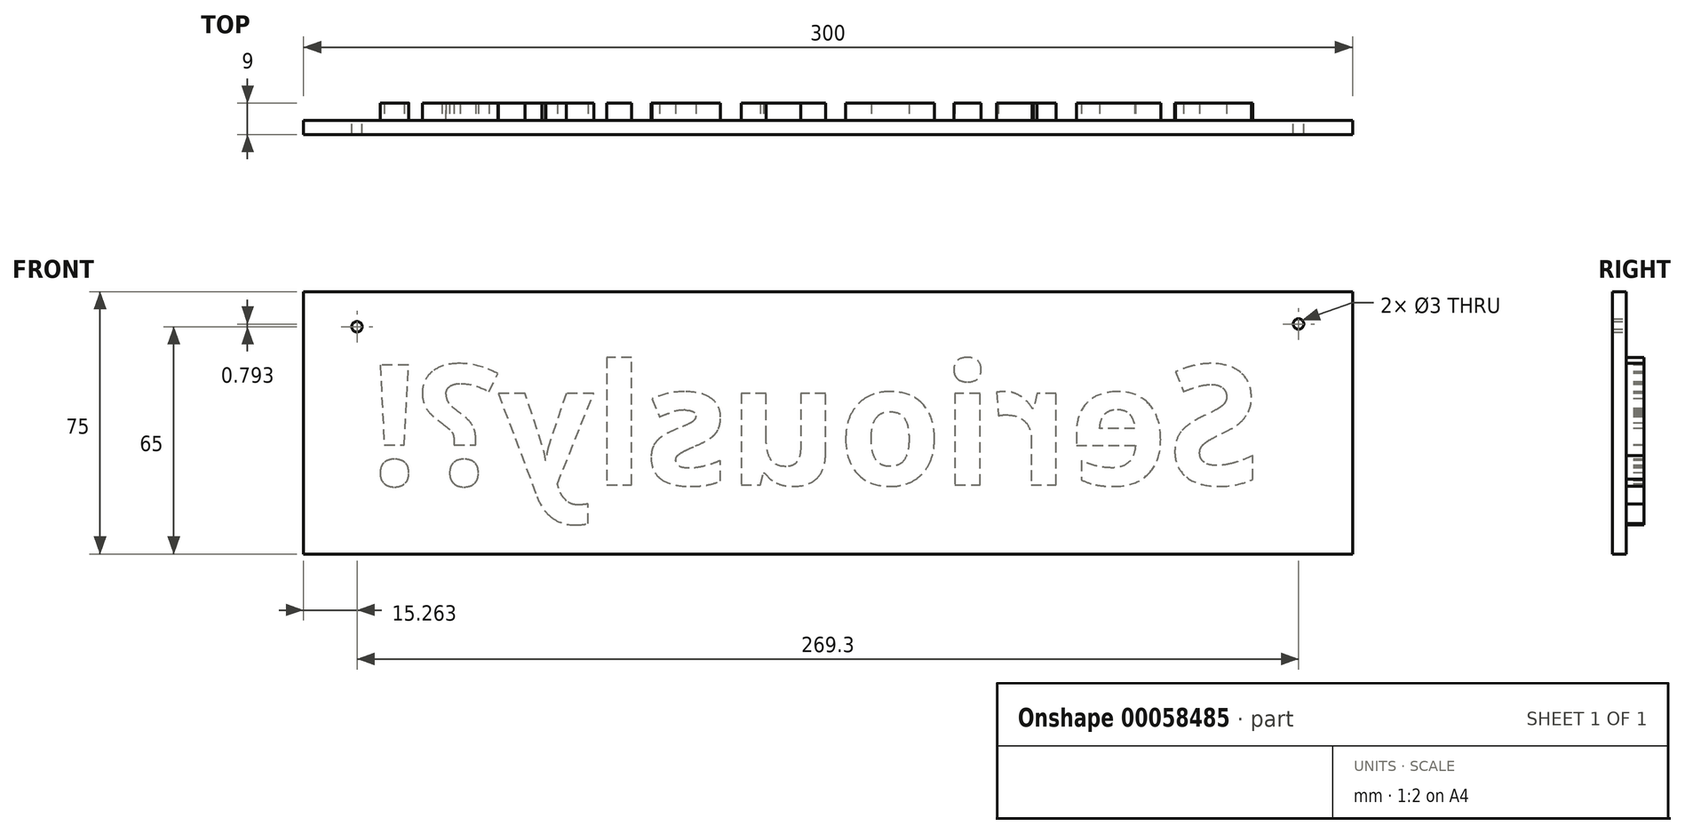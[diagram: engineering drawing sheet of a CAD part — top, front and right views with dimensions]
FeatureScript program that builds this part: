
annotation { "Feature Type Name" : "Feature", "Feature Type Description" : "" }
export const myFeature = defineFeature(function(context is Context, id is Id, definition is map)
    precondition{}
    {
        {
            var Q0;
            Q0=qCreatedBy(makeId("Front.planeOp"),FACE);
            var sketch = newSketch(context, id + "F0", { "sketchPlane" : qUnion([Q0])});
            skLineSegment(sketch, "E0.bottom", {"start": v(0, 0) * mm, "end": v(300, 0) * mm});
            skLineSegment(sketch, "E0.top", {"start": v(0, 75) * mm, "end": v(300, 75) * mm});
            skLineSegment(sketch, "E0.left", {"start": v(0, 0) * mm, "end": v(0, 75) * mm});
            skLineSegment(sketch, "E0.right", {"start": v(300, 0) * mm, "end": v(300, 75) * mm});
            skSolve(sketch);
        }
        {
            var Q0;
            Q0=makeQuery(id+"F0.imprint","IMPRINT",FACE,{"disambiguationData":[TD([[makeQuery(id+"F0.imprint","IMPRINT",EDGE,{"derivedFrom":sQuery(id+"F0.wireOp",EDGE,"E0.bottom")}),1.0]])]});
            extrude(context, id + "F1", {"entities" : qUnion([Q0]), "depth" : 4 * mm});
        }
        {
            var Q0;
            Q0=makeQuery(id+"F1.opExtrude","CAP_FACE",FACE,{"disambiguationData":[OSD([sQuery(id+"F0.wireOp",EDGE,"E0.bottom"),sQuery(id+"F0.wireOp",EDGE,"E0.top"),sQuery(id+"F0.wireOp",EDGE,"E0.left"),sQuery(id+"F0.wireOp",EDGE,"E0.right")])],"isStart":true});
            var sketch = newSketch(context, id + "F2", { "sketchPlane" : qUnion([Q0])});
            skText(sketch, "E1", { "text": "Seriously?!", "fontName": "OpenSans-Bold.ttf"});
            const initialGuessF2  = {"E1": [-0.27368, 0.01981, 1, 0, 0.03451]};
            skSetInitialGuess(sketch, initialGuessF2);
            skSolve(sketch);
        }
        {
            var Q0;
            Q0=makeQuery(id+"F2.imprint","IMPRINT",FACE,{"disambiguationData":[TD([[makeQuery(id+"F2.imprint","IMPRINT",EDGE,{"derivedFrom":sQuery(id+"F2.wireOp",EDGE,"E1.sketch_text.stroke-0")}),-1.0]])]});
            var Q1;
            Q1 = qSketchRegion(id + "F2", true);
            var Q2;
            Q2=makeQuery(id+"F2.imprint","IMPRINT",FACE,{"disambiguationData":[TD([[makeQuery(id+"F2.imprint","IMPRINT",EDGE,{"derivedFrom":sQuery(id+"F2.wireOp",EDGE,"E1.sketch_text.stroke-135")}),-1.0]])]});
            extrude(context, id + "F3", {"entities" : qUnion([Q0, Q1, Q2]), "operationType" : NewBodyOperationType.ADD, "depth" : 5 * mm});
        }
        {
            var Q0;
            {var subQ0=sQuery(id+"F0.wireOp",EDGE,"E0.left");var subQ1=sQuery(id+"F0.wireOp",EDGE,"E0.bottom");var subQ2=sQuery(id+"F0.wireOp",EDGE,"E0.right");var subQ3=sQuery(id+"F0.wireOp",EDGE,"E0.top");Q0=makeQuery(id+"F3.boolean.opBoolean","SPLIT",FACE,{"disambiguationData":[TD([makeQuery(id+"F1.opExtrude","SWEPT_FACE",FACE,{"disambiguationData":[OSD([subQ1])]})])],"derivedFrom":makeQuery(id+"F1.opExtrude","CAP_FACE",FACE,{"disambiguationData":[OSD([subQ1,subQ3,subQ0,subQ2])],"isStart":true})});}
            var sketch = newSketch(context, id + "F4", { "sketchPlane" : qUnion([Q0])});
            skPoint(sketch, "E2", {"position": v(-284.56, 65.8) * mm});
            skPoint(sketch, "E3", {"position": v(-10.99, 65.8) * mm});
            skSolve(sketch);
        }
        {
            var Q0;
            Q0=sQuery(id+"F4.wireOp",VERTEX,"E2");
            var Q1;
            Q1=makeQuery(id+"F1.opExtrude","SWEPT_BODY",BODY,{"disambiguationData":[OSD([sQuery(id+"F0.wireOp",EDGE,"E0.bottom"),sQuery(id+"F0.wireOp",EDGE,"E0.top"),sQuery(id+"F0.wireOp",EDGE,"E0.left"),sQuery(id+"F0.wireOp",EDGE,"E0.right")])]});
            hole(context, id + "F5", {"style" : HoleStyle.SIMPLE, "holeDiameter" : 3 * mm, "endStyle" : HoleEndStyle.THROUGH, "locations" : qUnion([Q0]), "scope" : qUnion([Q1])});
        }
        {
            var Q0;
            {var subQ0=sQuery(id+"F0.wireOp",EDGE,"E0.left");var subQ1=sQuery(id+"F0.wireOp",EDGE,"E0.bottom");var subQ2=sQuery(id+"F0.wireOp",EDGE,"E0.right");var subQ3=sQuery(id+"F0.wireOp",EDGE,"E0.top");Q0=makeQuery(id+"F3.boolean.opBoolean","SPLIT",FACE,{"disambiguationData":[TD([makeQuery(id+"F1.opExtrude","SWEPT_FACE",FACE,{"disambiguationData":[OSD([subQ1])]})])],"derivedFrom":makeQuery(id+"F1.opExtrude","CAP_FACE",FACE,{"disambiguationData":[OSD([subQ1,subQ3,subQ0,subQ2])],"isStart":true})});}
            var sketch = newSketch(context, id + "F6", { "sketchPlane" : qUnion([Q0])});
            skPoint(sketch, "E4", {"position": v(-15.26, 65) * mm});
            skSolve(sketch);
        }
        {
            var Q0;
            Q0=sQuery(id+"F6.wireOp",VERTEX,"E4");
            var Q1;
            Q1=makeQuery(id+"F1.opExtrude","SWEPT_BODY",BODY,{"disambiguationData":[OSD([sQuery(id+"F0.wireOp",EDGE,"E0.bottom"),sQuery(id+"F0.wireOp",EDGE,"E0.top"),sQuery(id+"F0.wireOp",EDGE,"E0.left"),sQuery(id+"F0.wireOp",EDGE,"E0.right")])]});
            hole(context, id + "F7", {"style" : HoleStyle.SIMPLE, "holeDiameter" : 3 * mm, "endStyle" : HoleEndStyle.THROUGH, "locations" : qUnion([Q0]), "scope" : qUnion([Q1])});
        }
    });
